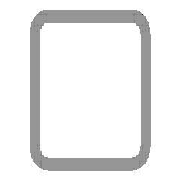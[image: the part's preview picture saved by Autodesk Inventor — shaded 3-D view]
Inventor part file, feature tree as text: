
AUTODESK INVENTOR PART (.ipt)
format: ipt  version: 2022 (Build 260153000, 153)  size: 652,288 bytes
history: native  units: mm (DEFAULTED — no unit token found)
features: other x8, sketch x5, plane x2, hole x2, surface_op x2, split x1
ambient origin geometry x8: Origin, YZ Plane, XZ Plane, XY Plane, X Axis, Y Axis, Z Axis, Center Point
bodies: Solid1 (feature_tree), Body (feature_tree), Solid7 (feature_tree), Solid8 (feature_tree)
feature tree (20):
  parser-record x1  (decoder bookkeeping rows leaked as tree rows — omitted from the tree; the rows remain in map.json)
  other  "Driven Length"
  other  "Start Plane"
  other  "End Plane"
  plane  "Work Plane4"
  split  "Split1"
  hole  "Hole1"  [1 undecoded]
  hole  "Hole2"  [1 undecoded]
  sketch  "Sketch"  dims[d13=-0.0mm d14=450.0mm d15=20.0mm d16=20.0mm d17=90.0deg d18=450.0mm d73=5.0mm d74=5.0mm d75=5.0mm d76=5.0mm d77=5.0mm d78=5.0mm d79=5.0mm d80=5.0mm d81=0.0mm d82=5.0mm d83=5.0mm d84=5.0mm d85=5.0mm d86=5.0mm d87=5.0mm d88=5.0mm d89=5.0mm d90=0.0mm d91=6.6mm d92=6.0mm d93=4.0mm d94=2.0mm d95=90.0deg d96=8.0mm d97=0.0mm d98=6.6mm d99=6.0mm d100=4.0mm d101=2.0mm d102=90.0deg d103=8.0mm d104=0.0mm]
  sketch  "Sketch3"  dims[d3=437.5mm d4=0.0mm]
  plane  "Work Plane3"
  sketch  "Sketch4"  dims[d7=4.0mm d9=40.0mm]
  other  "Srf13"
  other  "Srf14"
  sketch  "Sketch5"  dims[d11=40.0mm]
  sketch  "Sketch6"  dims[d12=2.0mm]
  other  "Srf12"
  surface_op  "Boundary Patch7"
  surface_op  "Boundary Patch8"
  other  "Srf15"
note: 2 required parameter values undecoded (feature->parameter linkage not recoverable at this tier; creation-order binding heuristic only, values carry confidence <= 0.55)
